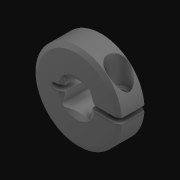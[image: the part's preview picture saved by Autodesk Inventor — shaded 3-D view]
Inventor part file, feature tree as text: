
AUTODESK INVENTOR PART (.ipt)
format: ipt  version: 2021 (Build 250183000, 183)  size: 164,352 bytes
history: native  units: in
note: dims shown in document units (in); Inventor stores cm internally (conversion verified against a paired STEP export)
features: mirror x1
ambient origin geometry x8: Origin, YZ Plane, XZ Plane, XY Plane, X Axis, Y Axis, Z Axis, Center Point
bodies: Solid1 (feature_tree)
feature tree (1):
  mirror  "Mirror1"
